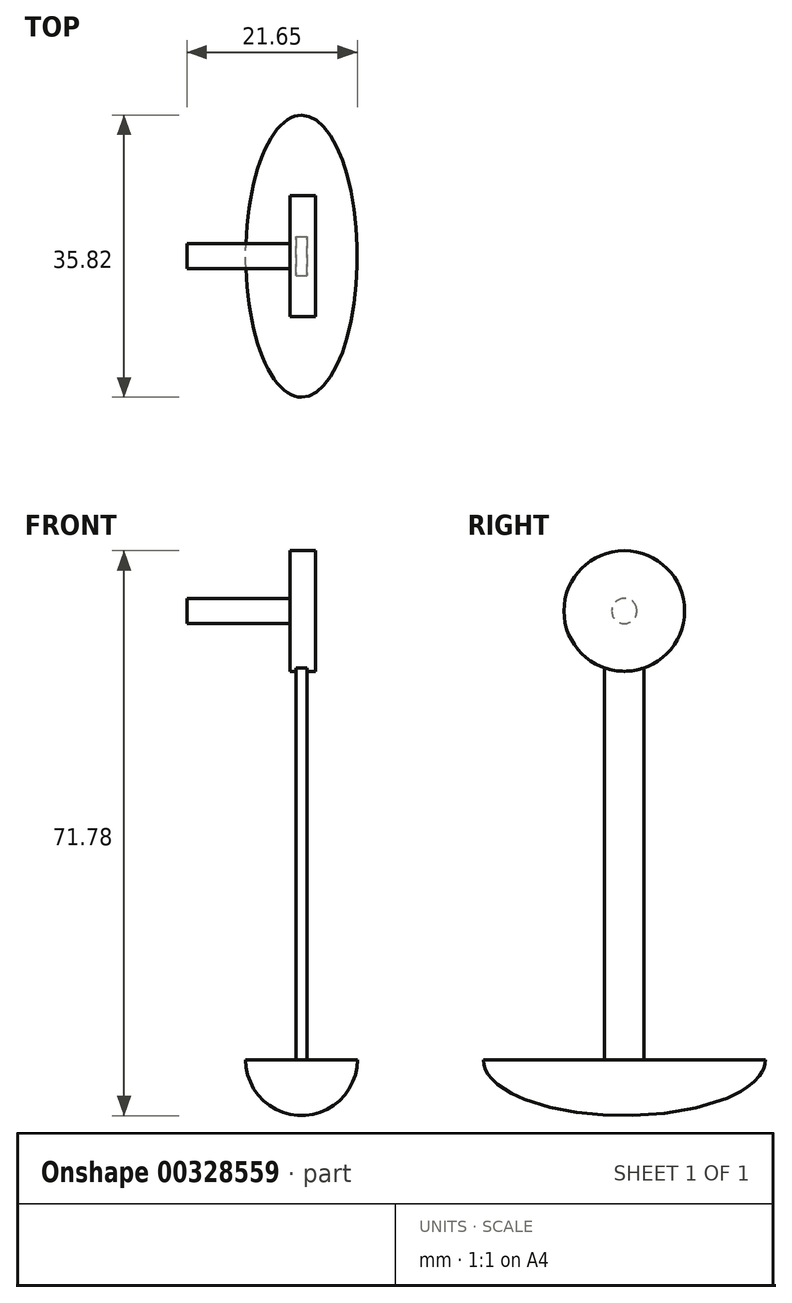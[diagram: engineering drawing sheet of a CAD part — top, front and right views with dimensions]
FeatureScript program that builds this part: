
annotation { "Feature Type Name" : "Feature", "Feature Type Description" : "" }
export const myFeature = defineFeature(function(context is Context, id is Id, definition is map)
    precondition{}
    {
        {
            var Q0;
            Q0=qCreatedBy(makeId("Front.planeOp"),FACE);
            var sketch = newSketch(context, id + "F0", { "sketchPlane" : qUnion([Q0])});
            skLineSegment(sketch, "E0.bottom", {"start": v(0, 67.45) * mm, "end": v(-13.11, 67.45) * mm});
            skLineSegment(sketch, "E0.left", {"start": v(0, 67.45) * mm, "end": v(0, 65.85) * mm});
            skLineSegment(sketch, "E1.top", {"start": v(-13.11, 73.5) * mm, "end": v(-16.36, 73.5) * mm});
            skLineSegment(sketch, "E1.left", {"start": v(-13.11, 65.85) * mm, "end": v(-13.11, 73.5) * mm});
            skLineSegment(sketch, "E1.right", {"start": v(-16.36, 65.85) * mm, "end": v(-16.36, 73.5) * mm});
            skPoint(sketch, "E1.middle", {"position": v(-13.85, 37.33) * mm});
            skLineSegment(sketch, "E2.bottom", {"start": v(-13.85, 8.82) * mm, "end": v(-15.27, 8.82) * mm});
            skLineSegment(sketch, "E2.left", {"start": v(-13.85, 8.82) * mm, "end": v(-13.85, 65.85) * mm});
            skLineSegment(sketch, "E2.right", {"start": v(-15.27, 8.82) * mm, "end": v(-15.27, 65.85) * mm});
            skPoint(sketch, "E2.middle", {"position": v(-13.85, 41.97) * mm});
            skPoint(sketch, "E3.endSnap0", {"position": v(-13.11, 65.85) * mm});
            skLineSegment(sketch, "E4", {"start": v(-16.36, 65.85) * mm, "end": v(0, 65.85) * mm});
            skLineSegment(sketch, "E5", {"start": v(-15.27, 65.85) * mm, "end": v(-13.85, 65.85) * mm});
            skSolve(sketch);
        }
        {
            var Q0;
            {var subQ3=sQuery(id+"F0.wireOp",EDGE,"E1.top");Q0=makeQuery(id+"F0.imprint","IMPRINT",FACE,{"disambiguationData":[TD([[makeQuery(id+"F0.imprint","IMPRINT",EDGE,{"derivedFrom":subQ3}),1.0]])]});}
            var Q1;
            {var subQ0=sQuery(id+"F0.wireOp",EDGE,"E0.bottom");Q1=makeQuery(id+"F0.imprint","IMPRINT",FACE,{"disambiguationData":[TD([[makeQuery(id+"F0.imprint","IMPRINT",EDGE,{"derivedFrom":subQ0}),1.0]])]});}
            var Q2;
            Q2=sQuery(id+"F0.wireOp",EDGE,"E4");
            revolve(context, id + "F1", {"entities" : qUnion([Q0, Q1]), "axis" : qUnion([Q2]), "revolveType" : RevolveType.FULL});
        }
        {
            var Q0;
            Q0=makeQuery(id+"F0.imprint","IMPRINT",FACE,{"disambiguationData":[TD([[makeQuery(id+"F0.imprint","IMPRINT",EDGE,{"derivedFrom":sQuery(id+"F0.wireOp",EDGE,"E2.bottom")}),-1.0]])]});
            extrude(context, id + "F2", {"entities" : qUnion([Q0]), "operationType" : NewBodyOperationType.ADD, "endBound" : BoundingType.SYMMETRIC, "depth" : 5 * mm});
        }
        {
            var Q0;
            Q0=makeQuery(id+"F2.opExtrude","SWEPT_FACE",FACE,{"disambiguationData":[OSD([sQuery(id+"F0.wireOp",EDGE,"E2.bottom")])]});
            cPlane(context, id + "F3", {"entities" : qUnion([Q0]), "cplaneType" : CPlaneType.OFFSET, "offset" : 0 * mm, "width" : 150 * mm, "height" : 150 * mm});
        }
        {
            var Q0;
            Q0=qCreatedBy(id+"F3.planeOp",FACE);
            var sketch = newSketch(context, id + "F4", { "sketchPlane" : qUnion([Q0])});
            skLineSegment(sketch, "E6", {"start": v(-13.7, 0) * mm, "end": v(-15.96, 0) * mm, "construction": true});
            skLineSegment(sketch, "E7", {"start": v(-14.56, -2.5) * mm, "end": v(-14.56, 2.5) * mm, "construction": true});
            skEllipticalArc(sketch, "E8", {});
            skLineSegment(sketch, "E9", {"start": v(-14.56, 2.5) * mm, "end": v(-14.56, 17.91) * mm});
            skLineSegment(sketch, "E10", {"start": v(-14.56, 17.91) * mm, "end": v(-14.56, -17.91) * mm});
            const initialGuessF4  = {"E8": [-0.014556926675140858, 0, 0, -1, 0.017911046743392944, 0.007092243835203478, 3.141592653589793, 0]};
            skSetInitialGuess(sketch, initialGuessF4);
            skSolve(sketch);
        }
        {
            var Q0;
            {var subQ0=sQuery(id+"F4.wireOp",EDGE,"E8");Q0=makeQuery(id+"F4.imprint","IMPRINT",FACE,{"disambiguationData":[TD([[makeQuery(id+"F4.imprint","IMPRINT",EDGE,{"derivedFrom":subQ0}),1.0]])]});}
            var Q1;
            Q1=sQuery(id+"F4.wireOp",EDGE,"E10");
            revolve(context, id + "F5", {"operationType" : NewBodyOperationType.ADD, "entities" : qUnion([Q0]), "axis" : qUnion([Q1]), "revolveType" : RevolveType.ONE_DIRECTION, "oppositeDirection" : true, "angle" : 180 * degree});
        }
        {
            var Q0;
            Q0=makeQuery(id+"F1.opRevolve","SWEPT_BODY",BODY,{"disambiguationData":[OSD([sQuery(id+"F0.wireOp",EDGE,"E0.bottom"),sQuery(id+"F0.wireOp",EDGE,"E0.left"),sQuery(id+"F0.wireOp",EDGE,"E1.top"),sQuery(id+"F0.wireOp",EDGE,"E1.left"),sQuery(id+"F0.wireOp",EDGE,"E1.right"),sQuery(id+"F0.wireOp",EDGE,"E4"),sQuery(id+"F0.wireOp",EDGE,"E5")])]});
            var Q1;
            Q1=qCreatedBy(makeId("Right.planeOp"),FACE);
            mirror(context, id + "F6", {"entities" : qUnion([Q0]), "mirrorPlane" : qUnion([Q1])});
        }
        {
            var Q0;
            Q0=makeQuery(id+"F1.opRevolve","SWEPT_BODY",BODY,{"disambiguationData":[OSD([sQuery(id+"F0.wireOp",EDGE,"E0.bottom"),sQuery(id+"F0.wireOp",EDGE,"E0.left"),sQuery(id+"F0.wireOp",EDGE,"E1.top"),sQuery(id+"F0.wireOp",EDGE,"E1.left"),sQuery(id+"F0.wireOp",EDGE,"E1.right"),sQuery(id+"F0.wireOp",EDGE,"E4"),sQuery(id+"F0.wireOp",EDGE,"E5")])]});
            deleteBodies(context, id + "F7", {"entities" : qUnion([Q0])});
        }
    });
